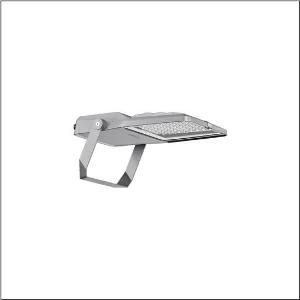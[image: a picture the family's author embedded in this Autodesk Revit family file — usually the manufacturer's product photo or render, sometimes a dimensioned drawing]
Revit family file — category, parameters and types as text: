
# Revit family: floodlight_fl_21_iq_mini___pl52_5xa7771b2d1a_9873
name_source: partatom
category: Lighting Fixtures
units: mm (PartAtom-declared; Revit-internal decimal feet)

## family parameters
Cut with Voids When Loaded = No
Host = Face
Light Source = No
Part Type = Normal
Room Calculation Point = No
Round Connector Dimension = Use Diameter
Shared = No

## types (1)
- --- (1 x LED, 6240 lm, 45.5 W, 3000K)
    Apparent Load = 46 VA
    CIE Flux Codes = 26 60 98 100 100
    Color Rendering = 70
    Color Temperature = 3000K
    Default Elevation = 1800 mm
    Description = Floodlight FL 21 iQ mini, floodlight, primary light control with lens, of PMMA, primary optical cover: protective disc, of toughened safety glass, transparent, light distribution: PL52, light emission: direct distribution, installation type: surface-mounted, LED, High Power LED, rated luminous flux: 6.240lm, luminous efficacy: 137lm/W, light colour: 730, colour temperature: 3000K, control: Auto-Match, Temp-Guard, Lumen-Switch, Night-Set, Smart-Wire, Light-Fading, Desk-Remote (wireless, voltage-free reading and setting of iQ features in the workshop via application-optimized NFC function/RFID function), optimised constant luminous flux control (CLO 2.0), with terminal, 6-pole, mains connection: 220..240V, AC, 50/60Hz, start of lifetime: 46W, end of service life: 48W, reduction: 22W, luminaire housing, of diecast aluminium, powder-coated, Siteco® metallic grey (DB 702S), corrosivity category C5 mid according to DIN EN ISO 12944, sealing non-destructively replaceable, mounting bracket, of steel, galvanised, powder-coated, Siteco® metallic grey (DB 702S), protection rating (complete): IP66, insulation class (complete): insulation class II (safety insulation), certification: CE, ENEC, VDE, protection symbol: D, impact resistance: IK08, permissible operating ambient temperature: -40..+40°C, permissible operating ambient temperature for outdoor applications: -40..+50°C, standard: DIN EN 12944, LABS conformity tested according to VDMA 24364:2018-05, packaging unit: 1 piece

Light Distribution: PL52
    Height = 70 mm
    Lamp = 1 x LED
    Lamp Light Flux = 6240 lm
    Lamp Power = 45.5 W
    Lamp count = 1
    Length = 485 mm
    Luminous efficacy = 137 lm/W
    Manufacturer = Siteco
    ModVariant = No
    Model = 5XA7771B2D1A
    Mounting Place = Wall
    Mounting Type = Surface mounted
    Number of Poles = 1
    OnlyDefault = Yes
    Power Factor = 1
    Product Name = Floodlight FL 21 iQ mini | PL52
    Product group = floodlight | wall mounted
    ProductGroupID = 2001
    Protection Class = Protection class II
    Protection Degree = IP 66
    RLX_Detail_Level = 1
    RLX_Emergency_Light_Flux = 0 lm
    RLX_Emergency_Type = 0
    RLX_Emergency_Type_DB = No
    RlxData = <blob elided: 96213 chars, md5=e0d9b991>
    Socket = socket
    Standby Power = 0 W
    System Light Flux = 6240 lm
    System Power = 46 W
    Type Comments = factory setting: luminous flux: 100 % | dim-lin: 254 | 463 mA
    Type Image = l_1006845.jpg
    URL = http://relux.com
    VarID = @adj_097467
    Voltage = 0 V
    Weight = 0.00 kg
    Width = 337 mm

## geometry (parser evidence)
native form markers: Blend x4, Sweep x12
no freeform markers — native parametric forms only
